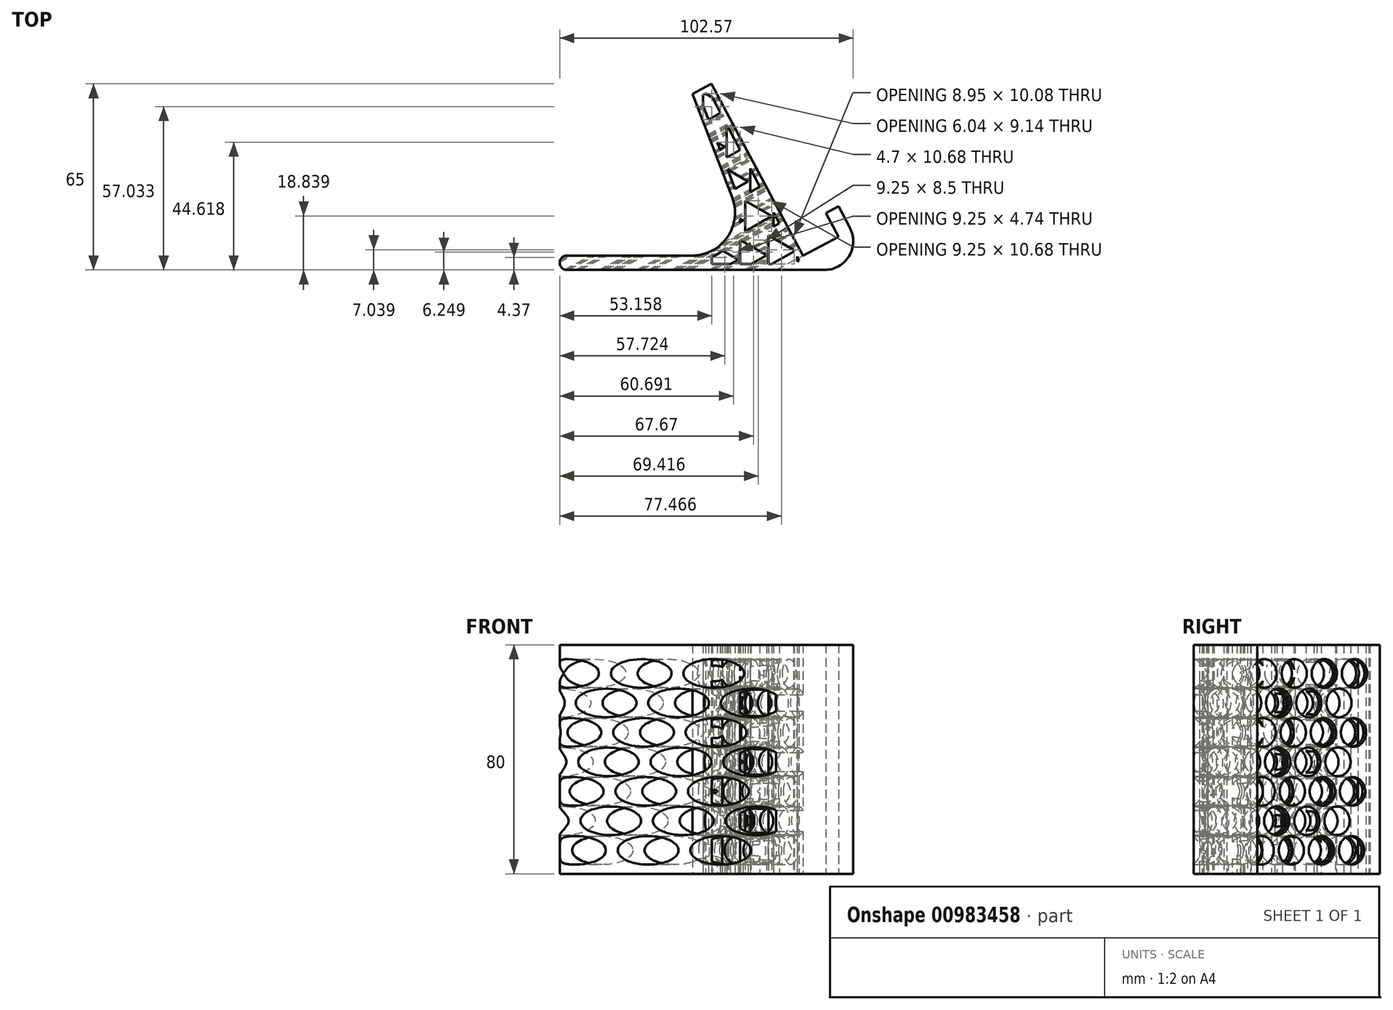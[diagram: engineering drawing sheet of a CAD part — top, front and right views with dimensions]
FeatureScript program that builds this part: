
annotation { "Feature Type Name" : "Feature", "Feature Type Description" : "" }
export const myFeature = defineFeature(function(context is Context, id is Id, definition is map)
    precondition{}
    {
        {
            var Q0;
            Q0=qCreatedBy(makeId("Top.planeOp"),FACE);
            var sketch = newSketch(context, id + "F0", { "sketchPlane" : qUnion([Q0])});
            skLineSegment(sketch, "E0.bottom", {"start": v(-46.7, -26.54) * mm, "end": v(43.37, -26.54) * mm});
            skLineSegment(sketch, "E0.left", {"start": v(-49.2, -24.04) * mm, "end": v(-49.2, -24.04) * mm});
            skLineSegment(sketch, "E1.0", {"start": v(-46.7, -21.54) * mm, "end": v(-2.96, -21.54) * mm});
            skLineSegment(sketch, "E2", {"start": v(3.84, 38.46) * mm, "end": v(35.84, -21.54) * mm});
            skLineSegment(sketch, "E3", {"start": v(35.84, -21.54) * mm, "end": v(48.2, -14.95) * mm});
            skLineSegment(sketch, "E4", {"start": v(48.2, -14.95) * mm, "end": v(43.78, -6.68) * mm});
            skLineSegment(sketch, "E5", {"start": v(43.78, -6.68) * mm, "end": v(48.2, -4.33) * mm});
            skLineSegment(sketch, "E6", {"start": v(48.2, -4.33) * mm, "end": v(52.2, -11.83) * mm});
            skPoint(sketch, "E7.newPointB", {"position": v(50.8, -26.54) * mm});
            skArc(sketch, "E7.filletArc", {"start": v(43.37, -26.54) * mm, "mid": v(51.95, -21.69) * mm, "end": v(52.2, -11.83) * mm});
            skArc(sketch, "E8.filletArc", {"start": v(-46.7, -21.54) * mm, "mid": v(-48.47, -22.27) * mm, "end": v(-49.2, -24.04) * mm});
            skPoint(sketch, "E9.visualSharp", {"position": v(-49.2, -26.54) * mm});
            skArc(sketch, "E9.filletArc", {"start": v(-49.2, -24.04) * mm, "mid": v(-48.47, -25.8) * mm, "end": v(-46.7, -26.54) * mm});
            skLineSegment(sketch, "E10", {"start": v(-2.78, 34.93) * mm, "end": v(3.84, 38.46) * mm});
            skLineSegment(sketch, "E11", {"start": v(-2.78, 34.93) * mm, "end": v(11.05, -1.18) * mm});
            skArc(sketch, "E12.filletArc", {"start": v(-2.96, -21.54) * mm, "mid": v(9.4, -15.04) * mm, "end": v(11.05, -1.18) * mm});
            skLineSegment(sketch, "E13.0", {"start": v(4.12, 33.68) * mm, "end": v(6.98, 28.33) * mm});
            skLineSegment(sketch, "E14.0", {"start": v(0.94, 30.82) * mm, "end": v(2.81, 25.92) * mm});
            skArc(sketch, "E15.0", {"start": v(3.9, -22.1) * mm, "mid": v(5.86, -21.07) * mm, "end": v(7.67, -19.8) * mm});
            skLineSegment(sketch, "E16.0", {"start": v(3.9, -24.54) * mm, "end": v(10.41, -24.54) * mm});
            skLineSegment(sketch, "E17", {"start": v(34.08, -22.48) * mm, "end": v(34.44, -23.16) * mm});
            skPoint(sketch, "E18.orphan", {"position": v(-46.7, -24.54) * mm});
            skLineSegment(sketch, "E19.0.3.0", {"start": v(8.44, 16.5) * mm, "end": v(6.79, 15.54) * mm});
            skLineSegment(sketch, "E19.0.4.2", {"start": v(1.72, 35.06) * mm, "end": v(4.12, 33.68) * mm});
            skLineSegment(sketch, "E19.1.0.0", {"start": v(13.15, -22.96) * mm, "end": v(10.41, -24.54) * mm});
            skLineSegment(sketch, "E19.1.1.0", {"start": v(14.9, -9.28) * mm, "end": v(13.69, -9.98) * mm});
            skLineSegment(sketch, "E19.1.2.0", {"start": v(16.64, 4.4) * mm, "end": v(12.06, 1.76) * mm});
            skLineSegment(sketch, "E19.1.2.2", {"start": v(9.47, 8.54) * mm, "end": v(16.64, 4.4) * mm});
            skLineSegment(sketch, "E19.1.3.1", {"start": v(9.14, 12.74) * mm, "end": v(9.14, 23.42) * mm});
            skLineSegment(sketch, "E19.1.3.2", {"start": v(9.14, 23.42) * mm, "end": v(9.8, 23.04) * mm});
            skLineSegment(sketch, "E19.2.0.0", {"start": v(23.1, -21.38) * mm, "end": v(17.62, -24.54) * mm});
            skLineSegment(sketch, "E19.2.0.2", {"start": v(13.85, -16.04) * mm, "end": v(23.1, -21.38) * mm});
            skLineSegment(sketch, "E19.2.1.0", {"start": v(24.84, -7.7) * mm, "end": v(15.6, -13.04) * mm});
            skLineSegment(sketch, "E19.2.1.1", {"start": v(15.6, -13.04) * mm, "end": v(15.6, -2.36) * mm});
            skLineSegment(sketch, "E19.2.1.2", {"start": v(15.6, -2.36) * mm, "end": v(24.84, -7.7) * mm});
            skLineSegment(sketch, "E19.2.2.1", {"start": v(17.34, 0.64) * mm, "end": v(17.34, 8.9) * mm});
            skLineSegment(sketch, "E19.3.0.0", {"start": v(32.74, -19.98) * mm, "end": v(24.83, -24.54) * mm});
            skLineSegment(sketch, "E19.3.0.1", {"start": v(23.8, -24.54) * mm, "end": v(23.8, -14.46) * mm});
            skLineSegment(sketch, "E19.3.0.2", {"start": v(23.8, -14.46) * mm, "end": v(32.47, -19.47) * mm});
            skLineSegment(sketch, "E19.3.1.1", {"start": v(25.54, -11.46) * mm, "end": v(25.54, -6.47) * mm});
            skLineSegment(sketch, "E19.4.0.0", {"start": v(34.44, -23.16) * mm, "end": v(33.74, -23.56) * mm});
            skLineSegment(sketch, "E19.4.0.1", {"start": v(33.74, -23.56) * mm, "end": v(33.74, -21.85) * mm});
            skLineSegment(sketch, "E19.direction1", {"start": v(-6.05, -29.88) * mm, "end": v(3.9, -28.3) * mm, "construction": true});
            skLineSegment(sketch, "E19.direction2", {"start": v(-6.05, -29.88) * mm, "end": v(-4.3, -16.2) * mm, "construction": true});
            skLineSegment(sketch, "E20.trimOffspring", {"start": v(3.9, -24.54) * mm, "end": v(3.9, -22.1) * mm});
            skLineSegment(sketch, "E21.trimOffspring", {"start": v(7.67, -19.8) * mm, "end": v(13.15, -22.96) * mm});
            skLineSegment(sketch, "E22.trimOffspring", {"start": v(13.85, -24.54) * mm, "end": v(13.85, -16.04) * mm});
            skLineSegment(sketch, "E23.trimOffspring", {"start": v(27.57, -10.29) * mm, "end": v(25.54, -11.46) * mm});
            skLineSegment(sketch, "E24.trimOffspring", {"start": v(13.9, -8.7) * mm, "end": v(14.9, -9.28) * mm});
            skLineSegment(sketch, "E25.trimOffspring", {"start": v(20.7, 2.58) * mm, "end": v(17.34, 0.64) * mm});
            skLineSegment(sketch, "E26.trimOffspring", {"start": v(13.84, 15.46) * mm, "end": v(9.14, 12.74) * mm});
            skLineSegment(sketch, "E27.trimOffspring", {"start": v(5.85, 18) * mm, "end": v(8.44, 16.5) * mm});
            skLineSegment(sketch, "E28.trimOffspring", {"start": v(6.98, 28.33) * mm, "end": v(2.81, 25.92) * mm});
            skLineSegment(sketch, "E29.trimOffspring", {"start": v(0.94, 30.82) * mm, "end": v(0.94, 34.65) * mm});
            skLineSegment(sketch, "E30.trimOffspring", {"start": v(13.85, -24.54) * mm, "end": v(17.62, -24.54) * mm});
            skArc(sketch, "E31.trimOffspring", {"start": v(13.69, -9.98) * mm, "mid": v(13.8, -9.34) * mm, "end": v(13.9, -8.7) * mm});
            skLineSegment(sketch, "E32.trimOffspring", {"start": v(23.8, -24.54) * mm, "end": v(24.83, -24.54) * mm});
            skLineSegment(sketch, "E33.trimOffspring", {"start": v(33.74, -21.85) * mm, "end": v(34.08, -22.48) * mm});
            skLineSegment(sketch, "E34.trimOffspring", {"start": v(32.47, -19.47) * mm, "end": v(32.74, -19.98) * mm});
            skLineSegment(sketch, "E35.trimOffspring", {"start": v(25.54, -6.47) * mm, "end": v(27.57, -10.29) * mm});
            skLineSegment(sketch, "E36.trimOffspring", {"start": v(17.34, 8.9) * mm, "end": v(20.7, 2.58) * mm});
            skLineSegment(sketch, "E37.trimOffspring", {"start": v(9.8, 23.04) * mm, "end": v(13.84, 15.46) * mm});
            skLineSegment(sketch, "E38", {"start": v(0.94, 34.65) * mm, "end": v(1.72, 35.06) * mm});
            skLineSegment(sketch, "E39.trimOffspring", {"start": v(5.85, 18) * mm, "end": v(6.79, 15.54) * mm});
            skLineSegment(sketch, "E40.trimOffspring", {"start": v(9.47, 8.54) * mm, "end": v(12.06, 1.76) * mm});
            skSolve(sketch);
        }
        {
            var Q0;
            Q0=makeQuery(id+"F0.imprint","IMPRINT",FACE,{"disambiguationData":[TD([[makeQuery(id+"F0.imprint","IMPRINT",EDGE,{"derivedFrom":sQuery(id+"F0.wireOp",EDGE,"E0.bottom")}),1.0]])]});
            extrude(context, id + "F1", {"entities" : qUnion([Q0]), "depth" : 80 * mm, "offsetDistance" : 25 * mm});
        }
        {
            var Q0;
            Q0=makeQuery(id+"F1.opExtrude","SWEPT_FACE",FACE,{"disambiguationData":[OSD([sQuery(id+"F0.wireOp",EDGE,"E2")])]});
            var sketch = newSketch(context, id + "F2", { "sketchPlane" : qUnion([Q0])});
            skCircle(sketch, "E41", {"center": v(22.13, 70) * mm, "radius": 5 * mm});
            skCircle(sketch, "E42.1.0.0", {"center": v(10.2, 70) * mm, "radius": 5 * mm});
            skCircle(sketch, "E42.1.1.0", {"center": v(15.97, 59.7) * mm, "radius": 5 * mm});
            skCircle(sketch, "E42.1.2.0", {"center": v(21.74, 49.4) * mm, "radius": 5 * mm});
            skCircle(sketch, "E42.2.0.0", {"center": v(-1.73, 70) * mm, "radius": 5 * mm});
            skCircle(sketch, "E42.2.1.0", {"center": v(4.04, 59.7) * mm, "radius": 5 * mm});
            skCircle(sketch, "E42.2.2.0", {"center": v(9.82, 49.4) * mm, "radius": 5 * mm});
            skCircle(sketch, "E42.2.3.0", {"center": v(15.59, 39.1) * mm, "radius": 5 * mm});
            skCircle(sketch, "E42.2.4.0", {"center": v(21.36, 28.8) * mm, "radius": 5 * mm});
            skCircle(sketch, "E42.3.0.0", {"center": v(-13.66, 70) * mm, "radius": 5 * mm});
            skCircle(sketch, "E42.3.1.0", {"center": v(-7.88, 59.7) * mm, "radius": 5 * mm});
            skCircle(sketch, "E42.3.2.0", {"center": v(-2.11, 49.4) * mm, "radius": 5 * mm});
            skCircle(sketch, "E42.3.3.0", {"center": v(3.66, 39.1) * mm, "radius": 5 * mm});
            skCircle(sketch, "E42.3.4.0", {"center": v(9.43, 28.8) * mm, "radius": 5 * mm});
            skCircle(sketch, "E42.3.5.0", {"center": v(15.2, 18.5) * mm, "radius": 5 * mm});
            skCircle(sketch, "E42.3.6.0", {"center": v(20.98, 8.2) * mm, "radius": 5 * mm});
            skCircle(sketch, "E42.4.0.0", {"center": v(-25.58, 70) * mm, "radius": 5 * mm});
            skCircle(sketch, "E42.4.1.0", {"center": v(-19.81, 59.7) * mm, "radius": 5 * mm});
            skCircle(sketch, "E42.4.2.0", {"center": v(-14.04, 49.4) * mm, "radius": 5 * mm});
            skCircle(sketch, "E42.4.3.0", {"center": v(-8.27, 39.1) * mm, "radius": 5 * mm});
            skCircle(sketch, "E42.4.4.0", {"center": v(-2.5, 28.8) * mm, "radius": 5 * mm});
            skCircle(sketch, "E42.4.5.0", {"center": v(3.28, 18.5) * mm, "radius": 5 * mm});
            skCircle(sketch, "E42.4.6.0", {"center": v(9.05, 8.2) * mm, "radius": 5 * mm});
            skCircle(sketch, "E42.5.1.0", {"center": v(-31.74, 59.7) * mm, "radius": 5 * mm});
            skCircle(sketch, "E42.5.2.0", {"center": v(-25.97, 49.4) * mm, "radius": 5 * mm});
            skCircle(sketch, "E42.5.3.0", {"center": v(-20.2, 39.1) * mm, "radius": 5 * mm});
            skCircle(sketch, "E42.5.4.0", {"center": v(-14.42, 28.8) * mm, "radius": 5 * mm});
            skCircle(sketch, "E42.5.5.0", {"center": v(-8.65, 18.5) * mm, "radius": 5 * mm});
            skCircle(sketch, "E42.5.6.0", {"center": v(-2.88, 8.2) * mm, "radius": 5 * mm});
            skCircle(sketch, "E42.6.3.0", {"center": v(-32.12, 39.1) * mm, "radius": 5 * mm});
            skCircle(sketch, "E42.6.4.0", {"center": v(-26.35, 28.8) * mm, "radius": 5 * mm});
            skCircle(sketch, "E42.6.5.0", {"center": v(-20.58, 18.5) * mm, "radius": 5 * mm});
            skCircle(sketch, "E42.6.6.0", {"center": v(-14.8, 8.2) * mm, "radius": 5 * mm});
            skCircle(sketch, "E42.7.5.0", {"center": v(-32.5, 18.5) * mm, "radius": 5 * mm});
            skCircle(sketch, "E42.7.6.0", {"center": v(-26.74, 8.2) * mm, "radius": 5 * mm});
            skLineSegment(sketch, "E42.direction1", {"start": v(22.13, 70) * mm, "end": v(10.2, 70) * mm, "construction": true});
            skLineSegment(sketch, "E42.direction2", {"start": v(22.13, 70) * mm, "end": v(27.9, 59.7) * mm, "construction": true});
            skSolve(sketch);
        }
        {
            var Q0;
            Q0=makeQuery(id+"F2.imprint","IMPRINT",FACE,{"disambiguationData":[TD([[makeQuery(id+"F2.imprint","IMPRINT",EDGE,{"derivedFrom":sQuery(id+"F2.wireOp",EDGE,"E42.3.6.0")}),1.0]])]});
            var Q1;
            Q1=makeQuery(id+"F2.imprint","IMPRINT",FACE,{"disambiguationData":[TD([[makeQuery(id+"F2.imprint","IMPRINT",EDGE,{"derivedFrom":sQuery(id+"F2.wireOp",EDGE,"E42.2.4.0")}),1.0]])]});
            var Q2;
            Q2=makeQuery(id+"F2.imprint","IMPRINT",FACE,{"disambiguationData":[TD([[makeQuery(id+"F2.imprint","IMPRINT",EDGE,{"derivedFrom":sQuery(id+"F2.wireOp",EDGE,"E42.3.5.0")}),1.0]])]});
            var Q3;
            Q3=makeQuery(id+"F2.imprint","IMPRINT",FACE,{"disambiguationData":[TD([[makeQuery(id+"F2.imprint","IMPRINT",EDGE,{"derivedFrom":sQuery(id+"F2.wireOp",EDGE,"E42.4.6.0")}),1.0]])]});
            var Q4;
            Q4=makeQuery(id+"F2.imprint","IMPRINT",FACE,{"disambiguationData":[TD([[makeQuery(id+"F2.imprint","IMPRINT",EDGE,{"derivedFrom":sQuery(id+"F2.wireOp",EDGE,"E42.4.5.0")}),1.0]])]});
            var Q5;
            Q5=makeQuery(id+"F2.imprint","IMPRINT",FACE,{"disambiguationData":[TD([[makeQuery(id+"F2.imprint","IMPRINT",EDGE,{"derivedFrom":sQuery(id+"F2.wireOp",EDGE,"E42.5.6.0")}),1.0]])]});
            var Q6;
            Q6=makeQuery(id+"F2.imprint","IMPRINT",FACE,{"disambiguationData":[TD([[makeQuery(id+"F2.imprint","IMPRINT",EDGE,{"derivedFrom":sQuery(id+"F2.wireOp",EDGE,"E42.5.5.0")}),1.0]])]});
            var Q7;
            Q7=makeQuery(id+"F2.imprint","IMPRINT",FACE,{"disambiguationData":[TD([[makeQuery(id+"F2.imprint","IMPRINT",EDGE,{"derivedFrom":sQuery(id+"F2.wireOp",EDGE,"E42.6.6.0")}),1.0]])]});
            var Q8;
            Q8=makeQuery(id+"F2.imprint","IMPRINT",FACE,{"disambiguationData":[TD([[makeQuery(id+"F2.imprint","IMPRINT",EDGE,{"derivedFrom":sQuery(id+"F2.wireOp",EDGE,"E42.6.5.0")}),1.0]])]});
            var Q9;
            Q9=makeQuery(id+"F2.imprint","IMPRINT",FACE,{"disambiguationData":[TD([[makeQuery(id+"F2.imprint","IMPRINT",EDGE,{"derivedFrom":sQuery(id+"F2.wireOp",EDGE,"E42.7.6.0")}),1.0]])]});
            var Q10;
            Q10=makeQuery(id+"F2.imprint","IMPRINT",FACE,{"disambiguationData":[TD([[makeQuery(id+"F2.imprint","IMPRINT",EDGE,{"derivedFrom":sQuery(id+"F2.wireOp",EDGE,"E42.6.4.0")}),1.0]])]});
            var Q11;
            {var subQ0=sQuery(id+"F2.wireOp",EDGE,"E42.6.3.0");var subQ1=makeQuery(id+"F1.opExtrude","SWEPT_EDGE",EDGE,{"disambiguationData":[OSD([sQuery(id+"F0.wireOp",EDGE,"E2"),sQuery(id+"F0.wireOp",EDGE,"E3")])]});var subQ2=makeQuery(id+"F2.imprint","INTERSECT",VERTEX,{"disambiguationData":[OD(0.0)],"derivedFrom":[subQ1,subQ0]});Q11=makeQuery(id+"F2.imprint","IMPRINT",FACE,{"disambiguationData":[TD([[makeQuery(id+"F2.imprint","IMPRINT",EDGE,{"disambiguationData":[TD([[subQ2,1.0]])],"derivedFrom":subQ0}),1.0]])]});}
            var Q12;
            {var subQ0=sQuery(id+"F2.wireOp",EDGE,"E42.5.1.0");var subQ1=makeQuery(id+"F1.opExtrude","SWEPT_EDGE",EDGE,{"disambiguationData":[OSD([sQuery(id+"F0.wireOp",EDGE,"E2"),sQuery(id+"F0.wireOp",EDGE,"E3")])]});var subQ2=makeQuery(id+"F2.imprint","INTERSECT",VERTEX,{"disambiguationData":[OD(0.0)],"derivedFrom":[subQ1,subQ0]});Q12=makeQuery(id+"F2.imprint","IMPRINT",FACE,{"disambiguationData":[TD([[makeQuery(id+"F2.imprint","IMPRINT",EDGE,{"disambiguationData":[TD([[subQ2,1.0]])],"derivedFrom":subQ0}),1.0]])]});}
            var Q13;
            Q13=makeQuery(id+"F2.imprint","IMPRINT",FACE,{"disambiguationData":[TD([[makeQuery(id+"F2.imprint","IMPRINT",EDGE,{"derivedFrom":sQuery(id+"F2.wireOp",EDGE,"E42.4.0.0")}),1.0]])]});
            var Q14;
            Q14=makeQuery(id+"F2.imprint","IMPRINT",FACE,{"disambiguationData":[TD([[makeQuery(id+"F2.imprint","IMPRINT",EDGE,{"derivedFrom":sQuery(id+"F2.wireOp",EDGE,"E42.3.0.0")}),1.0]])]});
            var Q15;
            Q15=makeQuery(id+"F2.imprint","IMPRINT",FACE,{"disambiguationData":[TD([[makeQuery(id+"F2.imprint","IMPRINT",EDGE,{"derivedFrom":sQuery(id+"F2.wireOp",EDGE,"E42.4.1.0")}),1.0]])]});
            var Q16;
            Q16=makeQuery(id+"F2.imprint","IMPRINT",FACE,{"disambiguationData":[TD([[makeQuery(id+"F2.imprint","IMPRINT",EDGE,{"derivedFrom":sQuery(id+"F2.wireOp",EDGE,"E42.4.2.0")}),1.0]])]});
            var Q17;
            Q17=makeQuery(id+"F2.imprint","IMPRINT",FACE,{"disambiguationData":[TD([[makeQuery(id+"F2.imprint","IMPRINT",EDGE,{"derivedFrom":sQuery(id+"F2.wireOp",EDGE,"E42.5.2.0")}),1.0]])]});
            var Q18;
            Q18=makeQuery(id+"F2.imprint","IMPRINT",FACE,{"disambiguationData":[TD([[makeQuery(id+"F2.imprint","IMPRINT",EDGE,{"derivedFrom":sQuery(id+"F2.wireOp",EDGE,"E42.5.3.0")}),1.0]])]});
            var Q19;
            Q19=makeQuery(id+"F2.imprint","IMPRINT",FACE,{"disambiguationData":[TD([[makeQuery(id+"F2.imprint","IMPRINT",EDGE,{"derivedFrom":sQuery(id+"F2.wireOp",EDGE,"E42.5.4.0")}),1.0]])]});
            var Q20;
            Q20=makeQuery(id+"F2.imprint","IMPRINT",FACE,{"disambiguationData":[TD([[makeQuery(id+"F2.imprint","IMPRINT",EDGE,{"derivedFrom":sQuery(id+"F2.wireOp",EDGE,"E42.4.3.0")}),1.0]])]});
            var Q21;
            Q21=makeQuery(id+"F2.imprint","IMPRINT",FACE,{"disambiguationData":[TD([[makeQuery(id+"F2.imprint","IMPRINT",EDGE,{"derivedFrom":sQuery(id+"F2.wireOp",EDGE,"E42.4.4.0")}),1.0]])]});
            var Q22;
            Q22=makeQuery(id+"F2.imprint","IMPRINT",FACE,{"disambiguationData":[TD([[makeQuery(id+"F2.imprint","IMPRINT",EDGE,{"derivedFrom":sQuery(id+"F2.wireOp",EDGE,"E42.3.1.0")}),1.0]])]});
            var Q23;
            Q23=makeQuery(id+"F2.imprint","IMPRINT",FACE,{"disambiguationData":[TD([[makeQuery(id+"F2.imprint","IMPRINT",EDGE,{"derivedFrom":sQuery(id+"F2.wireOp",EDGE,"E42.3.2.0")}),1.0]])]});
            var Q24;
            Q24=makeQuery(id+"F2.imprint","IMPRINT",FACE,{"disambiguationData":[TD([[makeQuery(id+"F2.imprint","IMPRINT",EDGE,{"derivedFrom":sQuery(id+"F2.wireOp",EDGE,"E42.3.3.0")}),1.0]])]});
            var Q25;
            Q25=makeQuery(id+"F2.imprint","IMPRINT",FACE,{"disambiguationData":[TD([[makeQuery(id+"F2.imprint","IMPRINT",EDGE,{"derivedFrom":sQuery(id+"F2.wireOp",EDGE,"E42.3.4.0")}),1.0]])]});
            var Q26;
            Q26=makeQuery(id+"F2.imprint","IMPRINT",FACE,{"disambiguationData":[TD([[makeQuery(id+"F2.imprint","IMPRINT",EDGE,{"derivedFrom":sQuery(id+"F2.wireOp",EDGE,"E42.2.3.0")}),1.0]])]});
            var Q27;
            Q27=makeQuery(id+"F2.imprint","IMPRINT",FACE,{"disambiguationData":[TD([[makeQuery(id+"F2.imprint","IMPRINT",EDGE,{"derivedFrom":sQuery(id+"F2.wireOp",EDGE,"E42.1.2.0")}),1.0]])]});
            var Q28;
            Q28=makeQuery(id+"F2.imprint","IMPRINT",FACE,{"disambiguationData":[TD([[makeQuery(id+"F2.imprint","IMPRINT",EDGE,{"derivedFrom":sQuery(id+"F2.wireOp",EDGE,"E42.2.2.0")}),1.0]])]});
            var Q29;
            Q29=makeQuery(id+"F2.imprint","IMPRINT",FACE,{"disambiguationData":[TD([[makeQuery(id+"F2.imprint","IMPRINT",EDGE,{"derivedFrom":sQuery(id+"F2.wireOp",EDGE,"E42.2.1.0")}),1.0]])]});
            var Q30;
            Q30=makeQuery(id+"F2.imprint","IMPRINT",FACE,{"disambiguationData":[TD([[makeQuery(id+"F2.imprint","IMPRINT",EDGE,{"derivedFrom":sQuery(id+"F2.wireOp",EDGE,"E42.2.0.0")}),1.0]])]});
            var Q31;
            Q31=makeQuery(id+"F2.imprint","IMPRINT",FACE,{"disambiguationData":[TD([[makeQuery(id+"F2.imprint","IMPRINT",EDGE,{"derivedFrom":sQuery(id+"F2.wireOp",EDGE,"E42.1.0.0")}),1.0]])]});
            var Q32;
            Q32=makeQuery(id+"F2.imprint","IMPRINT",FACE,{"disambiguationData":[TD([[makeQuery(id+"F2.imprint","IMPRINT",EDGE,{"derivedFrom":sQuery(id+"F2.wireOp",EDGE,"E42.1.1.0")}),1.0]])]});
            var Q33;
            Q33=makeQuery(id+"F2.imprint","IMPRINT",FACE,{"disambiguationData":[TD([[makeQuery(id+"F2.imprint","IMPRINT",EDGE,{"derivedFrom":sQuery(id+"F2.wireOp",EDGE,"E41")}),1.0]])]});
            var Q34;
            {var subQ0=sQuery(id+"F2.wireOp",EDGE,"E42.7.5.0");var subQ1=makeQuery(id+"F1.opExtrude","SWEPT_EDGE",EDGE,{"disambiguationData":[OSD([sQuery(id+"F0.wireOp",EDGE,"E2"),sQuery(id+"F0.wireOp",EDGE,"E3")])]});var subQ2=makeQuery(id+"F2.imprint","INTERSECT",VERTEX,{"disambiguationData":[OD(0.0)],"derivedFrom":[subQ1,subQ0]});Q34=makeQuery(id+"F2.imprint","IMPRINT",FACE,{"disambiguationData":[TD([[makeQuery(id+"F2.imprint","IMPRINT",EDGE,{"disambiguationData":[TD([[subQ2,-1.0]])],"derivedFrom":subQ0}),1.0]])]});}
            var Q35;
            Q35=sQuery(id+"F2.wireOp",EDGE,"E41");
            var Q36;
            Q36=sQuery(id+"F2.wireOp",EDGE,"E42.1.1.0");
            var Q37;
            Q37=sQuery(id+"F2.wireOp",EDGE,"E42.1.2.0");
            var Q38;
            Q38=sQuery(id+"F2.wireOp",EDGE,"E42.7.6.0");
            var Q39;
            Q39=sQuery(id+"F2.wireOp",EDGE,"E42.5.1.0");
            var Q40;
            Q40=sQuery(id+"F2.wireOp",EDGE,"E42.4.6.0");
            var Q41;
            Q41=sQuery(id+"F2.wireOp",EDGE,"E42.2.1.0");
            var Q42;
            Q42=sQuery(id+"F2.wireOp",EDGE,"E42.3.1.0");
            var Q43;
            Q43=sQuery(id+"F2.wireOp",EDGE,"E42.4.2.0");
            var Q44;
            Q44=sQuery(id+"F2.wireOp",EDGE,"E42.4.0.0");
            var Q45;
            Q45=sQuery(id+"F2.wireOp",EDGE,"E42.4.4.0");
            var Q46;
            Q46=sQuery(id+"F2.wireOp",EDGE,"E42.7.5.0");
            var Q47;
            Q47=sQuery(id+"F2.wireOp",EDGE,"E42.2.0.0");
            var Q48;
            Q48=sQuery(id+"F2.wireOp",EDGE,"E42.5.2.0");
            var Q49;
            Q49=sQuery(id+"F2.wireOp",EDGE,"E42.4.1.0");
            var Q50;
            Q50=sQuery(id+"F2.wireOp",EDGE,"E42.3.6.0");
            var Q51;
            Q51=sQuery(id+"F2.wireOp",EDGE,"E42.2.4.0");
            var Q52;
            Q52=sQuery(id+"F2.wireOp",EDGE,"E42.3.4.0");
            var Q53;
            Q53=sQuery(id+"F2.wireOp",EDGE,"E42.5.3.0");
            var Q54;
            Q54=sQuery(id+"F2.wireOp",EDGE,"E42.2.2.0");
            var Q55;
            Q55=sQuery(id+"F2.wireOp",EDGE,"E42.3.0.0");
            var Q56;
            Q56=sQuery(id+"F2.wireOp",EDGE,"E42.5.6.0");
            var Q57;
            Q57=sQuery(id+"F2.wireOp",EDGE,"E42.5.4.0");
            var Q58;
            Q58=sQuery(id+"F2.wireOp",EDGE,"E42.6.4.0");
            var Q59;
            Q59=sQuery(id+"F2.wireOp",EDGE,"E42.1.0.0");
            var Q60;
            Q60=sQuery(id+"F2.wireOp",EDGE,"E42.6.3.0");
            var Q61;
            Q61=sQuery(id+"F2.wireOp",EDGE,"E42.4.5.0");
            var Q62;
            Q62=sQuery(id+"F2.wireOp",EDGE,"E42.3.3.0");
            var Q63;
            Q63=sQuery(id+"F2.wireOp",EDGE,"E42.2.3.0");
            var Q64;
            Q64=sQuery(id+"F2.wireOp",EDGE,"E42.6.5.0");
            var Q65;
            Q65=sQuery(id+"F2.wireOp",EDGE,"E42.3.5.0");
            var Q66;
            Q66=sQuery(id+"F2.wireOp",EDGE,"E42.4.3.0");
            var Q67;
            Q67=sQuery(id+"F2.wireOp",EDGE,"E42.5.5.0");
            var Q68;
            Q68=sQuery(id+"F2.wireOp",EDGE,"E42.3.2.0");
            var Q69;
            Q69=sQuery(id+"F2.wireOp",EDGE,"E42.6.6.0");
            extrude(context, id + "F3", {"entities" : qUnion([Q0, Q1, Q2, Q3, Q4, Q5, Q6, Q7, Q8, Q9, Q10, Q11, Q12, Q13, Q14, Q15, Q16, Q17, Q18, Q19, Q20, Q21, Q22, Q23, Q24, Q25, Q26, Q27, Q28, Q29, Q30, Q31, Q32, Q33, Q34]), "operationType" : NewBodyOperationType.REMOVE, "surfaceOperationType" : NewSurfaceOperationType.ADD, "surfaceEntities" : qUnion([Q35, Q36, Q37, Q38, Q39, Q40, Q41, Q42, Q43, Q44, Q45, Q46, Q47, Q48, Q49, Q50, Q51, Q52, Q53, Q54, Q55, Q56, Q57, Q58, Q59, Q60, Q61, Q62, Q63, Q64, Q65, Q66, Q67, Q68, Q69]), "endBound" : BoundingType.THROUGH_ALL, "oppositeDirection" : true, "depth" : 25 * mm, "offsetDistance" : 25 * mm});
        }
    });
